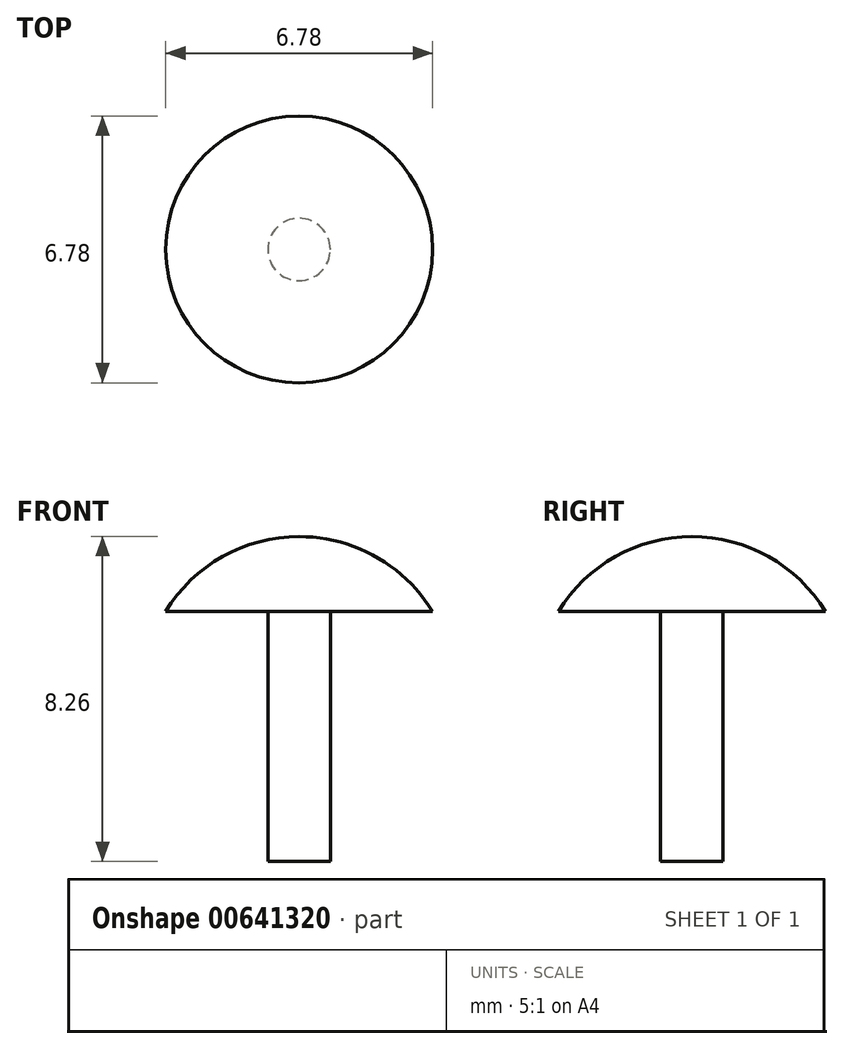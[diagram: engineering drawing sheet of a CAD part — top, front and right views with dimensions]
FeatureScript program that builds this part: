
annotation { "Feature Type Name" : "Feature", "Feature Type Description" : "" }
export const myFeature = defineFeature(function(context is Context, id is Id, definition is map)
    precondition{}
    {
        {
            var Q0;
            Q0=qCreatedBy(makeId("Front.planeOp"),FACE);
            var sketch = newSketch(context, id + "F0", { "sketchPlane" : qUnion([Q0])});
            skLineSegment(sketch, "E0", {"start": v(0, 0) * mm, "end": v(0.8, 0) * mm});
            skLineSegment(sketch, "E1", {"start": v(0.8, 0) * mm, "end": v(0.8, 6.35) * mm});
            skLineSegment(sketch, "E2", {"start": v(0, 0) * mm, "end": v(0, 7.31) * mm});
            skLineSegment(sketch, "E3", {"start": v(0, 0) * mm, "end": v(0, 8.26) * mm});
            skLineSegment(sketch, "E4", {"start": v(0, 8.26) * mm, "end": v(0, 4.29) * mm});
            skArc(sketch, "E5", {"start": v(0, 8.26) * mm, "mid": v(1.94, 7.75) * mm, "end": v(3.39, 6.35) * mm});
            skLineSegment(sketch, "E6", {"start": v(3.39, 6.35) * mm, "end": v(0.8, 6.35) * mm});
            skSolve(sketch);
        }
        {
            var Q0;
            Q0=makeQuery(id+"F0.imprint","IMPRINT",FACE,{"disambiguationData":[TD([[makeQuery(id+"F0.imprint","IMPRINT",EDGE,{"derivedFrom":sQuery(id+"F0.wireOp",EDGE,"E0")}),1.0]])]});
            var Q1;
            Q1=sQuery(id+"F0.wireOp",EDGE,"E3");
            revolve(context, id + "F1", {"entities" : qUnion([Q0]), "axis" : qUnion([Q1]), "revolveType" : RevolveType.FULL});
        }
    });
